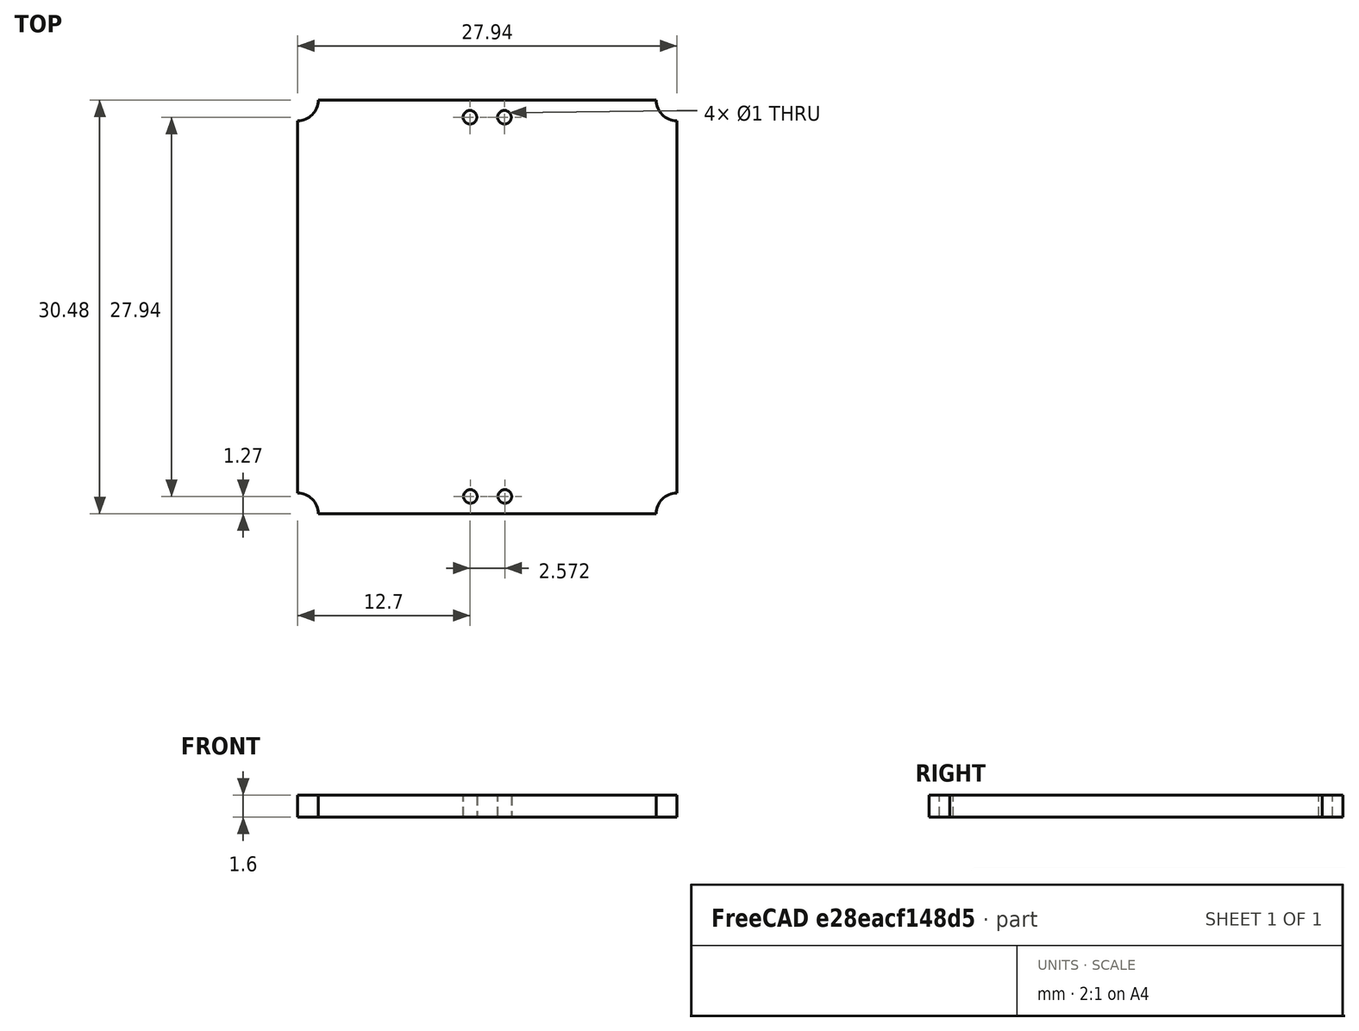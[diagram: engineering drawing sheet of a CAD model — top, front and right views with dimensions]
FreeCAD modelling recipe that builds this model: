
FCSTD DOCUMENT  (FreeCAD 0.16R6712 (Git))
Label: Backlight1
License: All rights reserved
LicenseURL: http://en.wikipedia.org/wiki/All_rights_reserved
objects: App::DocumentObjectGroup×2, Part::Feature×1, Sketcher::SketchObject×1
note: 2 computed .brp shape members not serialized (recipe doc carries the construction recipe); baked Part::Feature solids carry a one-line shape summary decoded from their .brp

FEATURE [Part::Feature] Pcb
  Placement = pos=(-90.17,91.44,0) rot=(0,0,1;0rad)
  shape: bbox 27.95 x 30.49 x 1.61 mm, 14 faces (baked)
FEATURE [Sketcher::SketchObject] PCB_Sketch
  sketch-geometry (8):
    g0: LineSegment StartX=-12.446 StartY=15.24 StartZ=0 EndX=12.446 EndY=15.24 EndZ=0
    g1: LineSegment StartX=-13.97 StartY=-13.716 StartZ=0 EndX=-13.97 EndY=13.716 EndZ=0
    g2: LineSegment StartX=12.446 StartY=-15.24 StartZ=0 EndX=-12.446 EndY=-15.24 EndZ=0
    g3: LineSegment StartX=13.97 StartY=13.716 StartZ=0 EndX=13.97 EndY=-13.716 EndZ=0
    g4: ArcOfCircle CenterX=-13.97 CenterY=15.24 CenterZ=0 NormalX=0 NormalY=0 NormalZ=1 Radius=1.524 StartAngle=4.71239 EndAngle=6.28319
    g5: ArcOfCircle CenterX=13.97 CenterY=15.24 CenterZ=0 NormalX=0 NormalY=0 NormalZ=1 Radius=1.524 StartAngle=3.14159 EndAngle=4.71239
    g6: ArcOfCircle CenterX=13.97 CenterY=-15.24 CenterZ=0 NormalX=0 NormalY=0 NormalZ=1 Radius=1.524 StartAngle=1.5708 EndAngle=3.14159
    g7: ArcOfCircle CenterX=-13.97 CenterY=-15.24 CenterZ=0 NormalX=0 NormalY=0 NormalZ=1 Radius=1.524 StartAngle=0 EndAngle=1.5708
  constraints (12):
    c: Horizontal(g0)
    c: Coincident(g0,g4)
    c: Coincident(g0,g5)
    c: Vertical(g1)
    c: Coincident(g1,g4)
    c: Coincident(g1,g7)
    c: Horizontal(g2)
    c: Coincident(g2,g6)
    c: Coincident(g2,g7)
    c: Vertical(g3)
    c: Coincident(g3,g5)
    c: Coincident(g3,g6)
FEATURE [App::DocumentObjectGroup] Board_Geoms
  Group = -> [Pcb,PCB_Sketch]
FEATURE [App::DocumentObjectGroup] Step_Models
